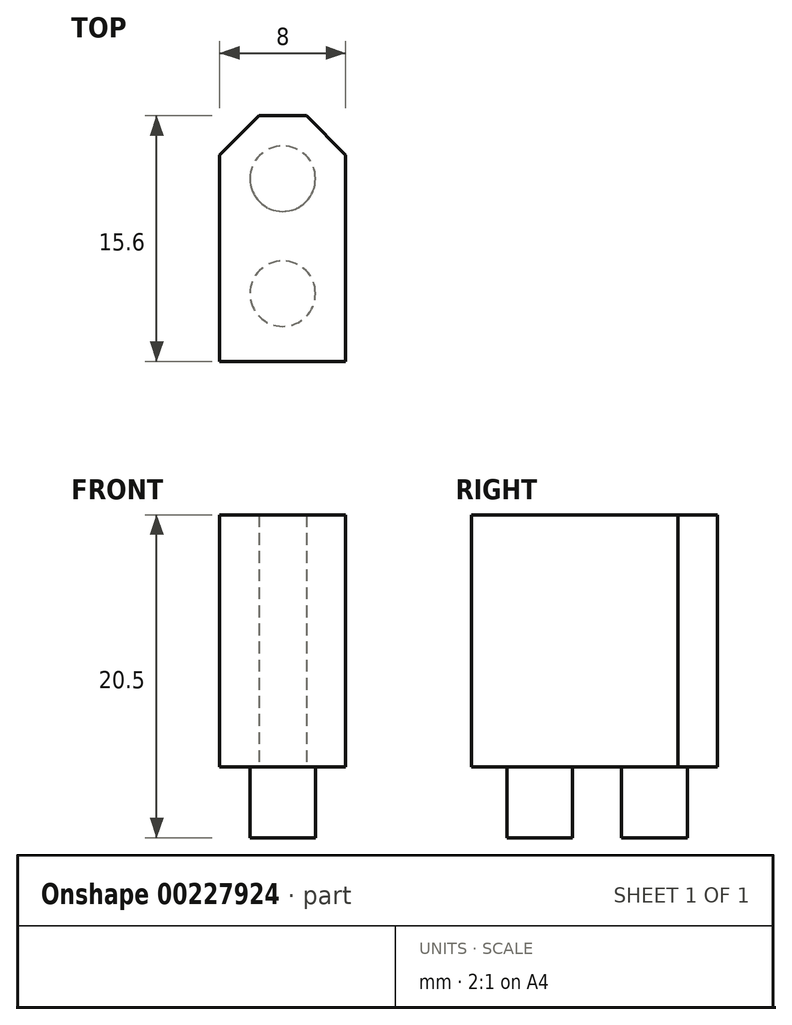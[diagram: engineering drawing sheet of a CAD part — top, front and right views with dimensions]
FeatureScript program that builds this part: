
annotation { "Feature Type Name" : "Feature", "Feature Type Description" : "" }
export const myFeature = defineFeature(function(context is Context, id is Id, definition is map)
    precondition{}
    {
        {
            var Q0;
            Q0=qCreatedBy(makeId("Top.planeOp"),FACE);
            var sketch = newSketch(context, id + "F0", { "sketchPlane" : qUnion([Q0])});
            skLineSegment(sketch, "E0.top", {"start": v(-4, 0) * mm, "end": v(4, 0) * mm});
            skLineSegment(sketch, "E0.left", {"start": v(-4, 13.1) * mm, "end": v(-4, 0) * mm});
            skLineSegment(sketch, "E0.right", {"start": v(4, 13.1) * mm, "end": v(4, 0) * mm});
            skLineSegment(sketch, "E1", {"start": v(-4, 13.1) * mm, "end": v(-1.5, 15.6) * mm});
            skLineSegment(sketch, "E2", {"start": v(-1.5, 15.6) * mm, "end": v(1.5, 15.6) * mm});
            skLineSegment(sketch, "E3", {"start": v(1.5, 15.6) * mm, "end": v(4, 13.1) * mm});
            skSolve(sketch);
        }
        {
            var Q0;
            Q0 = qSketchRegion(id + "F0", true);
            extrude(context, id + "F1", {"entities" : qUnion([Q0]), "depth" : 16 * mm});
        }
        {
            var Q0;
            Q0=makeQuery(id+"F1.opExtrude","CAP_FACE",FACE,{"disambiguationData":[OSD([sQuery(id+"F0.wireOp",EDGE,"E0.top"),sQuery(id+"F0.wireOp",EDGE,"E0.left"),sQuery(id+"F0.wireOp",EDGE,"E0.right"),sQuery(id+"F0.wireOp",EDGE,"E1"),sQuery(id+"F0.wireOp",EDGE,"E2"),sQuery(id+"F0.wireOp",EDGE,"E3")])],"isStart":true});
            var sketch = newSketch(context, id + "F2", { "sketchPlane" : qUnion([Q0])});
            skCircle(sketch, "E4", {"center": v(0, -4.31) * mm, "radius": 2.08 * mm});
            skCircle(sketch, "E5", {"center": v(0, -11.61) * mm, "radius": 2.08 * mm});
            skSolve(sketch);
        }
        {
            var Q0;
            Q0 = qSketchRegion(id + "F2", true);
            extrude(context, id + "F3", {"entities" : qUnion([Q0]), "operationType" : NewBodyOperationType.ADD, "depth" : 4.5 * mm});
        }
    });
